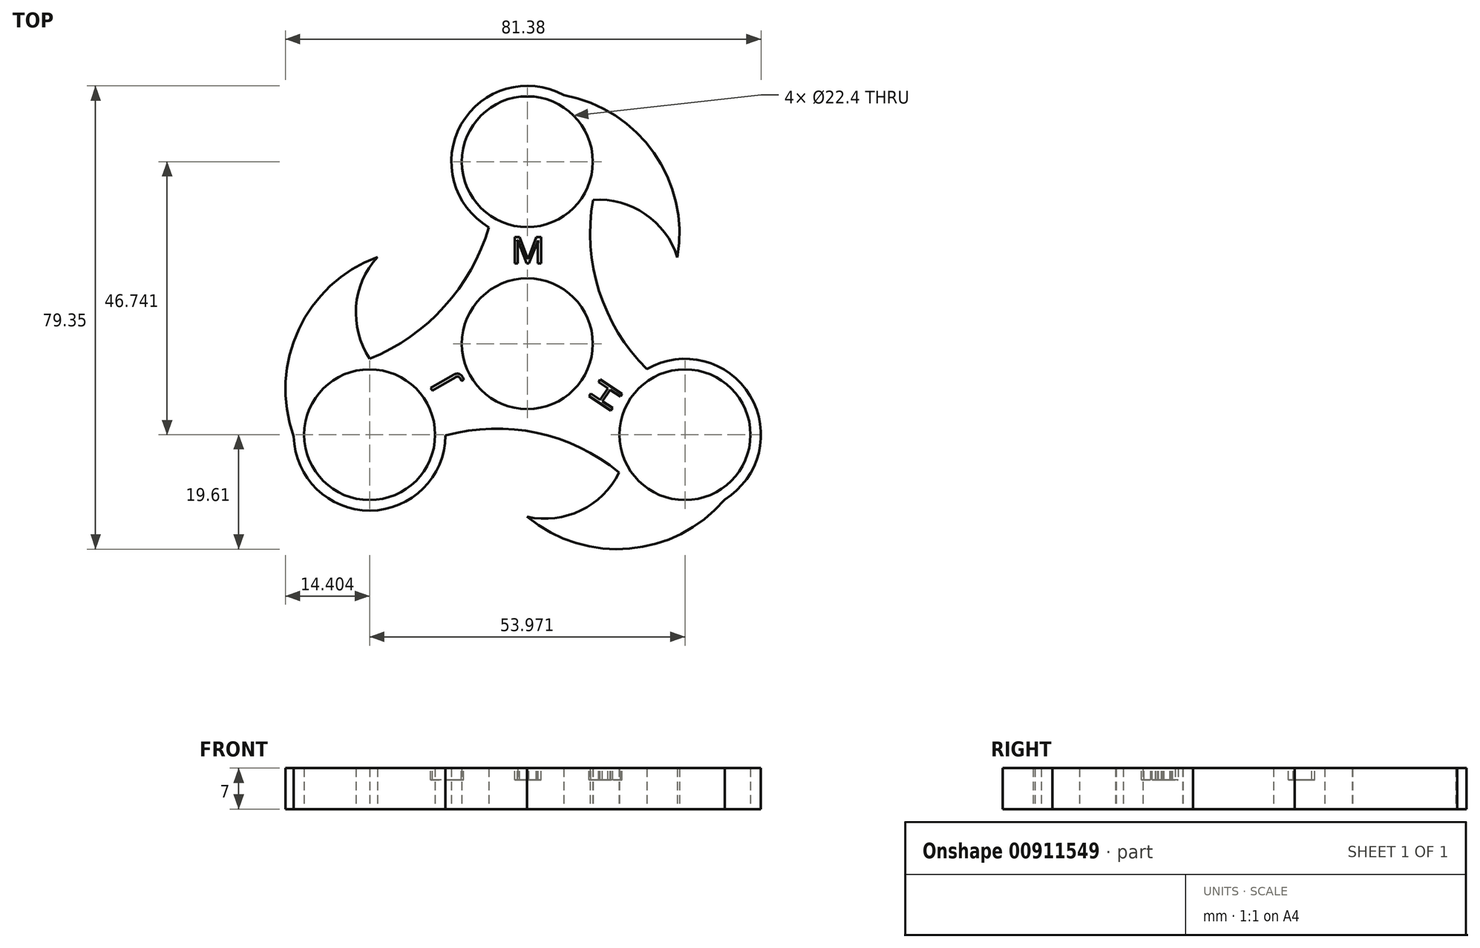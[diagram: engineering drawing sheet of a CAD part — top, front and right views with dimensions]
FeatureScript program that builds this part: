
annotation { "Feature Type Name" : "Feature", "Feature Type Description" : "" }
export const myFeature = defineFeature(function(context is Context, id is Id, definition is map)
    precondition{}
    {
        {
            var Q0;
            Q0=qCreatedBy(makeId("Top.planeOp"),FACE);
            var sketch = newSketch(context, id + "F0", { "sketchPlane" : qUnion([Q0])});
            skCircle(sketch, "E0", {"center": v(0, 0) * mm, "radius": 11.2 * mm});
            skCircle(sketch, "E1", {"center": v(0, 31.16) * mm, "radius": 11.2 * mm});
            skCircle(sketch, "E2", {"center": v(0, 31.16) * mm, "radius": 13 * mm});
            skCircle(sketch, "E3.1.0", {"center": v(-26.99, -15.58) * mm, "radius": 13 * mm});
            skCircle(sketch, "E4.1.0", {"center": v(-26.99, -15.58) * mm, "radius": 11.2 * mm});
            skCircle(sketch, "E4.2.0", {"center": v(26.99, -15.58) * mm, "radius": 11.2 * mm});
            skCircle(sketch, "E4.2.1", {"center": v(26.99, -15.58) * mm, "radius": 13 * mm});
            skArc(sketch, "E5", {"start": v(25.69, 14.79) * mm, "mid": v(21.66, 32.7) * mm, "end": v(6.2, 42.58) * mm});
            skArc(sketch, "E6", {"start": v(25.69, 14.79) * mm, "mid": v(20.16, 22.2) * mm, "end": v(11.24, 24.63) * mm});
            skArc(sketch, "E7.1.0", {"start": v(-25.64, 14.85) * mm, "mid": v(-29.3, 6.36) * mm, "end": v(-26.94, -2.58) * mm});
            skArc(sketch, "E7.1.1", {"start": v(-25.64, 14.85) * mm, "mid": v(-39.13, 2.41) * mm, "end": v(-39.97, -15.92) * mm});
            skArc(sketch, "E7.2.0", {"start": v(-0.03, -29.63) * mm, "mid": v(9.15, -28.56) * mm, "end": v(15.72, -22.04) * mm});
            skArc(sketch, "E7.2.1", {"start": v(-0.03, -29.63) * mm, "mid": v(17.49, -35.1) * mm, "end": v(33.78, -26.66) * mm});
            skArc(sketch, "E8", {"start": v(-26.94, -2.58) * mm, "mid": v(-14.2, 6.36) * mm, "end": v(-6.57, 19.94) * mm});
            skArc(sketch, "E9.1.0", {"start": v(15.72, -22.04) * mm, "mid": v(1.64, -15.26) * mm, "end": v(-13.99, -15.73) * mm});
            skArc(sketch, "E9.2.0", {"start": v(11.24, 24.63) * mm, "mid": v(12.38, 8.77) * mm, "end": v(20.8, -4.72) * mm});
            skSolve(sketch);
        }
        {
            var Q0;
            Q0=qSketchRegion(id+"F0",true);
            extrude(context, id + "F1", {"entities" : qUnion([Q0]), "depth" : 7 * mm, "offsetDistance" : 25 * mm});
        }
        {
            var Q0;
            Q0=makeQuery(id+"F1.opExtrude","CAP_FACE",FACE,{"disambiguationData":[OSD([sQuery(id+"F0.wireOp",EDGE,"E0"),sQuery(id+"F0.wireOp",EDGE,"E1"),sQuery(id+"F0.wireOp",EDGE,"E2"),sQuery(id+"F0.wireOp",EDGE,"E4.1.0"),sQuery(id+"F0.wireOp",EDGE,"E3.1.0"),sQuery(id+"F0.wireOp",EDGE,"E4.2.0"),sQuery(id+"F0.wireOp",EDGE,"E4.2.1"),sQuery(id+"F0.wireOp",EDGE,"E5"),sQuery(id+"F0.wireOp",EDGE,"E6"),sQuery(id+"F0.wireOp",EDGE,"E7.1.0"),sQuery(id+"F0.wireOp",EDGE,"E7.1.1"),sQuery(id+"F0.wireOp",EDGE,"E7.2.0"),sQuery(id+"F0.wireOp",EDGE,"E7.2.1"),sQuery(id+"F0.wireOp",EDGE,"E8"),sQuery(id+"F0.wireOp",EDGE,"E9.1.0"),sQuery(id+"F0.wireOp",EDGE,"E9.2.0")])],"isStart":false});
            var sketch = newSketch(context, id + "F2", { "sketchPlane" : qUnion([Q0])});
            skText(sketch, "E10", { "text": "M", "fontName": "OpenSans-Regular.ttf"});
            skText(sketch, "E11", { "text": "J", "fontName": "OpenSans-Regular.ttf"});
            skText(sketch, "E12", { "text": "H", "fontName": "OpenSans-Regular.ttf"});
            skLineSegment(sketch, "E13", {"start": v(0, 13.74) * mm, "end": v(0, 11.2) * mm});
            skLineSegment(sketch, "E14", {"start": v(-12.6, -5.41) * mm, "end": v(-10.4, -4.14) * mm, "construction": true});
            skLineSegment(sketch, "E15", {"start": v(11.44, -7.6) * mm, "end": v(9.33, -6.2) * mm, "construction": true});
            skLineSegment(sketch, "E16", {"start": v(10.2, -9.45) * mm, "end": v(7.91, -7.93) * mm, "construction": true});
            skLineSegment(sketch, "E17", {"start": v(12.67, -5.75) * mm, "end": v(10.37, -4.23) * mm, "construction": true});
            const initialGuessF2  = {"E10": [-0.00274, 0.01374, 1, 0, 0.00454], "E11": [-0.0121, -0.00628, -0.5, 0.86603, 0.00452], "E12": [0.01399, -0.01197, 0.5536, 0.83279, 0.00454]};
            skSetInitialGuess(sketch, initialGuessF2);
            skSolve(sketch);
        }
        {
            var Q0;
            Q0 = qSketchRegion(id + "F2", true);
            extrude(context, id + "F3", {"entities" : qUnion([Q0]), "operationType" : NewBodyOperationType.REMOVE, "oppositeDirection" : true, "depth" : 2 * mm, "offsetDistance" : 25 * mm});
        }
    });
